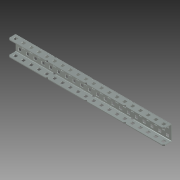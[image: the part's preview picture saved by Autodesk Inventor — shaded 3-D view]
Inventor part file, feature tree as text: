
AUTODESK INVENTOR PART (.ipt)
format: ipt  version: 2013 (Build 170138000, 138)  size: 1,319,424 bytes
history: native  units: in
note: dims shown in document units (in); Inventor stores cm internally (conversion verified against a paired STEP export)
features: other x109, extrude x99, sketch x12, pattern_linear x8, sheet_metal_op x7, mirror x3, plane x2, projected_geometry x2
ambient origin geometry x8: Origin, YZ Plane, XZ Plane, XY Plane, X Axis, Y Axis, Z Axis, Center Point
bodies: Solid1 (feature_tree)
feature tree (242):
  sheet_metal_op  "Face1"
  sheet_metal_op  "Flange1"
  sketch  "Sketch3"  dims[d2=0.032in]
  pattern_linear  "Rectangular Pattern1"  Spacing1=0.078in  [1 undecoded]
  pattern_linear  "Rectangular Pattern2"  Spacing1=0.182in  [1 undecoded]
  pattern_linear  "Rectangular Pattern3"  Spacing1=0.182in  [1 undecoded]
  pattern_linear  "Rectangular Pattern4"  Spacing1=0.159in  [1 undecoded]
  plane  "Work Plane1"
  sheet_metal_op  "Flange2"
  other  "Corner Chamfer1"
  pattern_linear  "Rectangular Pattern8"  Spacing1=0.02in  [1 undecoded]
  plane  "Work Plane2"
  mirror  "Mirror3"
  pattern_linear  "Rectangular Pattern9"  Spacing1=0.046in  [1 undecoded]
  mirror  "Mirror4"
  pattern_linear  "Rectangular Pattern10"  Spacing1=0.0in  [1 undecoded]
  pattern_linear  "Rectangular Pattern11"  Count1=20 Spacing1=0.5in
  mirror  "Mirror6"
  sketch  "Sketch1"  dims[d0=10.0in]
  other  "Plate1"
  sketch  "Sketch2"  dims[d1=0.546in]
  other  "Plate2"
  sheet_metal_op  "Bend1"
  sheet_metal_op  "Corner1"
  projected_geometry  "Projected Loop1"
  projected_geometry  "Projected Loop2"
  sketch  "Sketch4"  dims[d3=0.046in]
  sketch  "Sketch5"  dims[d4=0.023in]
  sketch  "Sketch6"  dims[d5=0.092in]
  other  "Srf1"
  other  "Srf2"
  other  "Srf3"
  other  "Srf4"
  other  "Srf5"
  other  "Srf6"
  other  "Srf7"
  other  "Srf8"
  other  "Srf9"
  other  "Srf10"
  other  "Srf11"
  other  "Srf12"
  other  "Srf13"
  other  "Srf14"
  other  "Srf15"
  other  "Srf16"
  other  "Srf17"
  other  "Srf18"
  other  "Srf19"
  other  "Srf20"
  other  "Srf21"
  other  "Srf22"
  other  "Srf23"
  other  "Srf24"
  other  "Srf25"
  other  "Srf26"
  other  "Srf27"
  other  "Srf28"
  other  "Srf29"
  other  "Srf30"
  other  "Srf31"
  other  "Srf32"
  other  "Srf33"
  other  "Srf34"
  other  "Srf35"
  other  "Srf36"
  other  "Srf37"
  other  "Srf38"
  other  "Srf39"
  other  "Srf40"
  sketch  "Sketch7"  dims[d6=0.032in]
  other  "Srf401"
  other  "Srf402"
  other  "Srf403"
  other  "Srf404"
  other  "Srf405"
  other  "Srf406"
  other  "Srf407"
  other  "Srf408"
  other  "Srf409"
  other  "Srf410"
  other  "Srf411"
  other  "Srf412"
  other  "Srf413"
  other  "Srf414"
  other  "Srf415"
  other  "Srf416"
  other  "Srf417"
  other  "Srf418"
  other  "Srf419"
  other  "Work Axis1"
  sketch  "Sketch8"  dims[d7=0.954in d8=90.0deg d9=0.032in]
  sketch  "Sketch11"  dims[d10=0.184in]
  other  "Plate3"
  sheet_metal_op  "Bend2"
  sheet_metal_op  "Corner2"
  sketch  "Sketch12"  dims[d11=0.046in]
  sketch  "Sketch13"  dims[d12=0.032in]
  sketch  "Sketch14"  dims[d13=0.032in d14=0.078in d15=0.182in d16=0.182in d18=0.159in d19=0.02in d20=0.046in d21=0.0in d22=7.874in d24=0.5in d25=0.7874in d27=0.5in d28=0.182in d29=0.182in d30=0.25in d31=0.25in d32=0.046in d33=0.0in d34=0.02in d35=7.4803in d37=0.5in d38=1.0in d39=0.0in d40=7.874in d42=0.5in d43=0.7874in d45=0.5in d46=1.0in d47=0.0in d48=7.4803in d50=0.5in d51=135.0deg d52=0.0in d53=0.0in d54=0.0in d55=0.0in d56=0.0in d57=0.0in d58=0.0in d59=0.0in d60=0.0in d61=0.0in d62=0.0in d63=0.0in d64=0.0in d65=0.0in d66=0.0in d67=0.0in d68=0.0in d69=0.0in d70=0.0in d71=0.0in d72=0.0in d73=0.0in d74=0.0in d75=0.0in d76=0.0in d77=0.0in d78=0.0in d79=0.0in d80=0.0in d81=0.0in d82=0.0in d83=0.0in d84=0.0in d85=0.0in d86=0.0in d87=0.0in d88=0.0in d89=0.0in d90=0.0in d91=0.0in d92=0.0in d93=0.0in d94=0.0in d95=0.0in d96=0.0in d97=0.0in d98=0.0in d99=0.0in d100=0.0in d101=0.0in d102=0.0in d103=0.0in d104=0.0in d105=0.0in d106=0.0in d107=0.0in d108=0.0in d109=0.0in d110=0.0in d111=0.0in d112=0.0in d113=0.0in d114=0.0in d115=0.0in d116=0.0in d117=0.0in d118=0.0in d119=0.0in d120=0.0in d121=0.0in d122=0.0in d123=0.0in d124=0.0in d125=0.0in d126=0.0in d127=0.0in d128=0.0in d129=0.0in d130=0.0in d131=0.0in d132=0.0in d133=0.0in d134=0.0in d135=0.0in d136=0.0in d137=0.0in d138=0.0in d139=0.0in d140=0.0in d141=0.0in d142=0.0in d143=0.0in d144=0.0in d145=0.0in d146=0.0in d147=0.0in d148=0.0in d149=0.0in d150=0.0in d151=0.0in d152=0.0in d153=0.0in d154=0.0in d155=0.0in d156=0.0in d157=0.0in d158=0.0in d159=0.0in d160=0.0in d161=0.0in d162=0.0in d163=0.0in d164=0.0in d165=0.0in d166=0.0in d167=0.0in d168=0.0in d169=0.0in d170=0.09in d171=0.25in d172=45.0deg d316=0.046in d317=0.023in d318=0.092in d319=0.032in d320=0.546in d321=90.0deg d322=0.032in d323=0.184in d324=0.046in d325=0.032in d326=0.581in d330=0.078in d331=0.039in d333=0.046in d334=0.6508in d335=0.046in d336=0.0in d337=1.1811in d339=2.5in d340=90.0deg d341=0.16in d342=0.046in d343=0.0in d344=1.1811in d346=2.5in d347=0.206in d348=0.182in d349=0.02in d350=0.159in d351=0.046in d352=0.0in d353=7.874in d355=0.5in d356=1.0in d357=0.0in d358=7.874in d360=0.5in d361=0.0in d362=0.0in d363=0.0in d364=0.0in d365=0.0in d366=0.0in d367=0.0in d368=0.0in d369=0.0in d370=0.0in d371=0.0in d372=0.0in d373=0.0in d374=0.0in d375=0.0in d376=0.0in d377=0.0in d378=0.0in d379=0.0in d380=0.0in d381=0.0in d382=0.0in d383=0.0in d384=0.0in d385=0.0in d386=0.0in d387=0.0in d388=0.0in d389=0.0in d390=0.0in d391=0.0in d392=0.0in d393=0.0in d394=0.0in d395=0.0in d396=0.0in d397=0.0in d398=0.0in d399=0.0in d400=0.0in d401=0.0in d402=0.0in d403=0.0in d404=0.0in d405=0.0in d406=0.0in d407=0.0in d408=0.0in d409=0.0in d410=0.0in d411=0.0in d412=0.0in d413=0.0in d414=0.0in d415=0.0in d416=0.0in d417=0.0in d418=0.0in d419=0.0in d420=0.0in d421=0.0in d422=0.0in d423=0.0in d424=0.0in d425=0.0in d426=0.0in d427=0.0in d428=0.0in d429=0.0in d430=0.0in d431=0.0in d432=0.0in d433=0.0in d434=0.0in d435=0.0in d436=0.0in d437=0.0in d438=0.0in d439=0.0in d440=0.0in]
  other  "Srf479"
  other  "Srf480"
  other  "Srf481"
  other  "Srf482"
  other  "Srf483"
  other  "Srf484"
  other  "Srf485"
  other  "Srf486"
  other  "Srf487"
  other  "Srf488"
  other  "Srf489"
  other  "Srf490"
  other  "Srf491"
  other  "Srf492"
  other  "Srf493"
  other  "Srf494"
  other  "Srf495"
  other  "Srf496"
  other  "Srf497"
  other  "Srf498"
  other  "Srf519"
  other  "Srf520"
  other  "Srf521"
  other  "Srf522"
  other  "Srf523"
  other  "Srf524"
  other  "Srf525"
  other  "Srf526"
  other  "Srf527"
  other  "Srf528"
  other  "Srf529"
  other  "Srf530"
  other  "Srf531"
  other  "Srf532"
  other  "Srf533"
  other  "Srf534"
  other  "Srf535"
  other  "Srf536"
  other  "Srf537"
  other  "Srf538"
  other  "Cut1"
  other  "Cut2"
  extrude  "ExtrusionSrf1"  Depth=0.7874in
  extrude  "ExtrusionSrf401"  Depth=0.182in
  other  "Cut6"
  other  "Cut7"
  other  "Cut8"
  extrude  "ExtrusionSrf479"  Depth=0.182in
  extrude  "ExtrusionSrf2"  Depth=0.25in
  extrude  "ExtrusionSrf3"  Depth=0.25in
  extrude  "ExtrusionSrf4"  Depth=0.046in
  extrude  "ExtrusionSrf5"  TaperAngle=0.0deg  [1 undecoded]
  extrude  "ExtrusionSrf6"  Depth=0.02in
  extrude  "ExtrusionSrf7"  Depth=7.4803in
  extrude  "ExtrusionSrf8"  Depth=1.0in TaperAngle=0.0deg
  extrude  "ExtrusionSrf9"  Depth=7.874in
  extrude  "ExtrusionSrf10"  Depth=1.0in TaperAngle=0.0deg
  extrude  "ExtrusionSrf11"  Depth=7.4803in
  extrude  "ExtrusionSrf12"  Depth=0.046in
  extrude  "ExtrusionSrf13"  Depth=0.023in
  extrude  "ExtrusionSrf14"  Depth=0.092in
  extrude  "ExtrusionSrf15"  Depth=0.032in
  extrude  "ExtrusionSrf16"  Depth=0.546in TaperAngle=90.0deg
  extrude  "ExtrusionSrf17"  Depth=0.184in
  extrude  "ExtrusionSrf18"  Depth=0.046in
  extrude  "ExtrusionSrf19"  Depth=0.032in
  extrude  "ExtrusionSrf20"  Depth=0.581in
  extrude  "ExtrusionSrf21"  Depth=0.078in
  extrude  "ExtrusionSrf22"  Depth=0.039in
  extrude  "ExtrusionSrf23"  Depth=0.046in
  extrude  "ExtrusionSrf24"  Depth=0.6508in
  extrude  "ExtrusionSrf25"  Depth=0.046in
  extrude  "ExtrusionSrf26"  TaperAngle=0.0deg  [1 undecoded]
  extrude  "ExtrusionSrf27"  Depth=1.1811in
  extrude  "ExtrusionSrf28"  TaperAngle=90.0deg  [1 undecoded]
  extrude  "ExtrusionSrf29"  Depth=0.16in
  extrude  "ExtrusionSrf30"  Depth=0.046in
  extrude  "ExtrusionSrf31"  TaperAngle=0.0deg  [1 undecoded]
  extrude  "ExtrusionSrf32"  Depth=1.1811in
  extrude  "ExtrusionSrf33"  Depth=0.206in
  extrude  "ExtrusionSrf34"  Depth=0.182in
  extrude  "ExtrusionSrf35"  Depth=0.02in
  extrude  "ExtrusionSrf36"  Depth=0.159in
  extrude  "ExtrusionSrf37"  Depth=0.046in
  extrude  "ExtrusionSrf38"  TaperAngle=0.0deg  [1 undecoded]
  extrude  "ExtrusionSrf39"  Depth=7.874in
  extrude  "ExtrusionSrf40"  Depth=1.0in TaperAngle=0.0deg
  extrude  "ExtrusionSrf402"  Depth=7.874in
  extrude  "ExtrusionSrf403"  [1 undecoded]
  extrude  "ExtrusionSrf404"  [1 undecoded]
  extrude  "ExtrusionSrf405"  [1 undecoded]
  extrude  "ExtrusionSrf406"  [1 undecoded]
  extrude  "ExtrusionSrf407"  [1 undecoded]
  extrude  "ExtrusionSrf408"  [1 undecoded]
  extrude  "ExtrusionSrf409"  [1 undecoded]
  extrude  "ExtrusionSrf410"  [1 undecoded]
  extrude  "ExtrusionSrf411"  [1 undecoded]
  extrude  "ExtrusionSrf412"  [1 undecoded]
  extrude  "ExtrusionSrf413"  [1 undecoded]
  extrude  "ExtrusionSrf414"  [1 undecoded]
  extrude  "ExtrusionSrf415"  [1 undecoded]
  extrude  "ExtrusionSrf416"  [1 undecoded]
  extrude  "ExtrusionSrf417"  [1 undecoded]
  extrude  "ExtrusionSrf418"  [1 undecoded]
  extrude  "ExtrusionSrf419"  [1 undecoded]
  extrude  "ExtrusionSrf480"  [1 undecoded]
  extrude  "ExtrusionSrf481"  [1 undecoded]
  extrude  "ExtrusionSrf482"  [1 undecoded]
  extrude  "ExtrusionSrf483"  [1 undecoded]
  extrude  "ExtrusionSrf484"  [1 undecoded]
  extrude  "ExtrusionSrf485"  [1 undecoded]
  extrude  "ExtrusionSrf486"  [1 undecoded]
  extrude  "ExtrusionSrf487"  [1 undecoded]
  extrude  "ExtrusionSrf488"  [1 undecoded]
  extrude  "ExtrusionSrf489"  [1 undecoded]
  extrude  "ExtrusionSrf490"  [1 undecoded]
  extrude  "ExtrusionSrf491"  [1 undecoded]
  extrude  "ExtrusionSrf492"  [1 undecoded]
  extrude  "ExtrusionSrf493"  [1 undecoded]
  extrude  "ExtrusionSrf494"  [1 undecoded]
  extrude  "ExtrusionSrf495"  [1 undecoded]
  extrude  "ExtrusionSrf496"  [1 undecoded]
  extrude  "ExtrusionSrf497"  [1 undecoded]
  extrude  "ExtrusionSrf498"  [1 undecoded]
  extrude  "ExtrusionSrf519"  [1 undecoded]
  extrude  "ExtrusionSrf520"  [1 undecoded]
  extrude  "ExtrusionSrf521"  [1 undecoded]
  extrude  "ExtrusionSrf522"  [1 undecoded]
  extrude  "ExtrusionSrf523"  [1 undecoded]
  extrude  "ExtrusionSrf524"  [1 undecoded]
  extrude  "ExtrusionSrf525"  [1 undecoded]
  extrude  "ExtrusionSrf526"  [1 undecoded]
  extrude  "ExtrusionSrf527"  [1 undecoded]
  extrude  "ExtrusionSrf528"  [1 undecoded]
  extrude  "ExtrusionSrf529"  [1 undecoded]
  extrude  "ExtrusionSrf530"  [1 undecoded]
  extrude  "ExtrusionSrf531"  [1 undecoded]
  extrude  "ExtrusionSrf532"  [1 undecoded]
  extrude  "ExtrusionSrf533"  [1 undecoded]
  extrude  "ExtrusionSrf534"  [1 undecoded]
  extrude  "ExtrusionSrf535"  [1 undecoded]
  extrude  "ExtrusionSrf536"  [1 undecoded]
  extrude  "ExtrusionSrf537"  [1 undecoded]
  extrude  "ExtrusionSrf538"  [1 undecoded]
note: 68 required parameter values undecoded (feature->parameter linkage not recoverable at this tier; creation-order binding heuristic only, values carry confidence <= 0.55)
